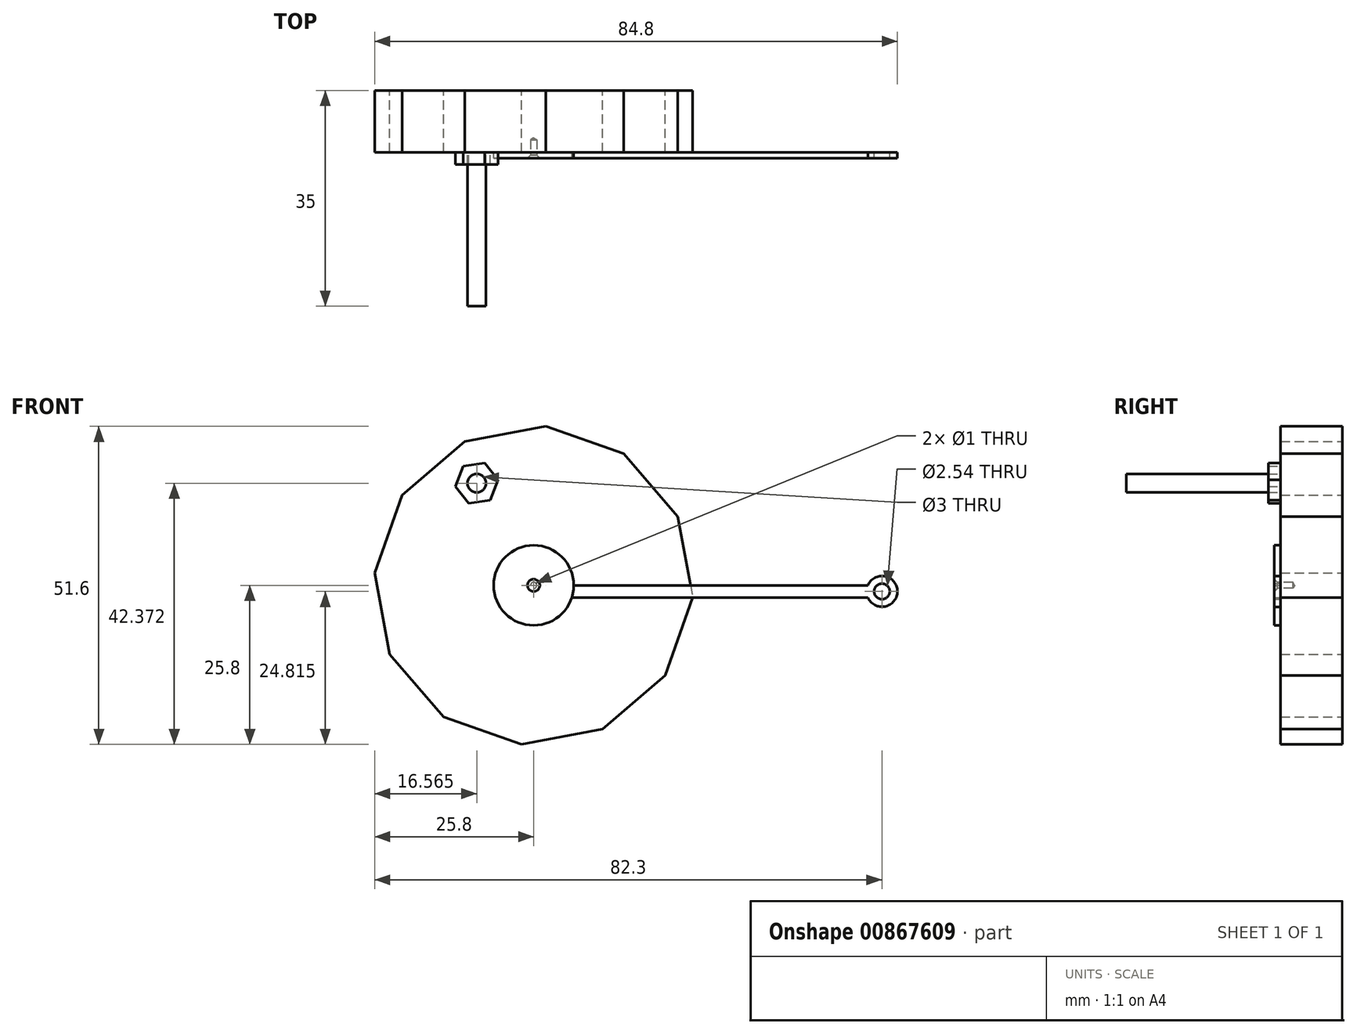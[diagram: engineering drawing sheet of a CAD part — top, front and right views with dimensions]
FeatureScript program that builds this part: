
annotation { "Feature Type Name" : "Feature", "Feature Type Description" : "" }
export const myFeature = defineFeature(function(context is Context, id is Id, definition is map)
    precondition{}
    {
        {
            var Q0;
            Q0=qCreatedBy(makeId("Front.planeOp"),FACE);
            var sketch = newSketch(context, id + "F0", { "sketchPlane" : qUnion([Q0])});
            skCircle(sketch, "E0.cCircle", {"center": v(0, 0) * mm, "radius": 25 * mm, "construction": true});
            skLineSegment(sketch, "E0.0", {"start": v(-21.35, 14.63) * mm, "end": v(-11.17, 23.35) * mm});
            skLineSegment(sketch, "E0.1", {"start": v(-11.17, 23.35) * mm, "end": v(2, 25.8) * mm});
            skLineSegment(sketch, "E0.2", {"start": v(2, 25.8) * mm, "end": v(14.63, 21.35) * mm});
            skLineSegment(sketch, "E0.3", {"start": v(14.63, 21.35) * mm, "end": v(23.35, 11.17) * mm});
            skLineSegment(sketch, "E0.4", {"start": v(23.35, 11.17) * mm, "end": v(25.8, -2) * mm});
            skLineSegment(sketch, "E0.5", {"start": v(25.8, -2) * mm, "end": v(21.35, -14.63) * mm});
            skLineSegment(sketch, "E0.6", {"start": v(21.35, -14.63) * mm, "end": v(11.17, -23.35) * mm});
            skLineSegment(sketch, "E0.7", {"start": v(11.17, -23.35) * mm, "end": v(-2, -25.8) * mm});
            skLineSegment(sketch, "E0.8", {"start": v(-2, -25.8) * mm, "end": v(-14.63, -21.35) * mm});
            skLineSegment(sketch, "E0.9", {"start": v(-14.63, -21.35) * mm, "end": v(-23.35, -11.17) * mm});
            skLineSegment(sketch, "E0.10", {"start": v(-23.35, -11.17) * mm, "end": v(-25.8, 2) * mm});
            skLineSegment(sketch, "E0.11", {"start": v(-25.8, 2) * mm, "end": v(-21.35, 14.63) * mm});
            skPoint(sketch, "E0.0.midPoint", {"position": v(-16.26, 19) * mm});
            skSolve(sketch);
        }
        {
            var Q0;
            Q0=makeQuery(id+"F0.imprint","IMPRINT",FACE,{"disambiguationData":[TD([[makeQuery(id+"F0.imprint","IMPRINT",EDGE,{"derivedFrom":sQuery(id+"F0.wireOp",EDGE,"E0.0")}),-1.0]])]});
            extrude(context, id + "F1", {"entities" : qUnion([Q0]), "depth" : 10 * mm, "offsetDistance" : 25 * mm});
        }
        {
            var Q0;
            Q0=makeQuery(id+"F1.opExtrude","CAP_FACE",FACE,{"disambiguationData":[OSD([sQuery(id+"F0.wireOp",EDGE,"E0.0"),sQuery(id+"F0.wireOp",EDGE,"E0.1"),sQuery(id+"F0.wireOp",EDGE,"E0.2"),sQuery(id+"F0.wireOp",EDGE,"E0.3"),sQuery(id+"F0.wireOp",EDGE,"E0.4"),sQuery(id+"F0.wireOp",EDGE,"E0.5"),sQuery(id+"F0.wireOp",EDGE,"E0.6"),sQuery(id+"F0.wireOp",EDGE,"E0.7"),sQuery(id+"F0.wireOp",EDGE,"E0.8"),sQuery(id+"F0.wireOp",EDGE,"E0.9"),sQuery(id+"F0.wireOp",EDGE,"E0.10"),sQuery(id+"F0.wireOp",EDGE,"E0.11")])],"isStart":false});
            var sketch = newSketch(context, id + "F2", { "sketchPlane" : qUnion([Q0])});
            skCircle(sketch, "E1", {"center": v(0, 0) * mm, "radius": 6.5 * mm});
            skLineSegment(sketch, "E2", {"start": v(6.5, 0) * mm, "end": v(56.5, 0) * mm});
            skLineSegment(sketch, "E3", {"start": v(6.2, -1.97) * mm, "end": v(56.5, -1.97) * mm});
            skLineSegment(sketch, "E4", {"start": v(56.5, 0) * mm, "end": v(56.5, -1.97) * mm});
            skCircle(sketch, "E5", {"center": v(56.5, -0.99) * mm, "radius": 2.5 * mm});
            skCircle(sketch, "E6", {"center": v(56.5, -0.99) * mm, "radius": 1.27 * mm});
            skSolve(sketch);
        }
        {
            var Q0;
            {var subQ0=sQuery(id+"F2.wireOp",EDGE,"E1");var subQ1=makeQuery(id+"F2.imprint","INTERSECT",VERTEX,{"derivedFrom":[subQ0,sQuery(id+"F2.wireOp",EDGE,"E2")]});Q0=makeQuery(id+"F2.imprint","IMPRINT",FACE,{"disambiguationData":[TD([[makeQuery(id+"F2.imprint","IMPRINT",EDGE,{"disambiguationData":[TD([[subQ1,-1.0]])],"derivedFrom":subQ0}),1.0]])]});}
            extrude(context, id + "F3", {"entities" : qUnion([Q0]), "depth" : 1 * mm, "offsetDistance" : 25 * mm});
        }
        {
            var Q0;
            {var subQ1=sQuery(id+"F2.wireOp",EDGE,"E2");var subQ6=makeQuery(id+"F1.opExtrude","CAP_EDGE",EDGE,{"disambiguationData":[OSD([sQuery(id+"F0.wireOp",EDGE,"E0.4")])],"isStart":false});var subQ8=makeQuery(id+"F2.imprint","INTERSECT",VERTEX,{"derivedFrom":[subQ6,subQ1]});Q0=makeQuery(id+"F2.imprint","IMPRINT",FACE,{"disambiguationData":[TD([[makeQuery(id+"F2.imprint","IMPRINT",EDGE,{"disambiguationData":[TD([[subQ8,-1.0]])],"derivedFrom":subQ6}),-1.0]])]});}
            var Q1;
            {var subQ0=sQuery(id+"F2.wireOp",EDGE,"E5");var subQ1=sQuery(id+"F2.wireOp",EDGE,"E2");var subQ2=makeQuery(id+"F2.imprint","INTERSECT",VERTEX,{"derivedFrom":[subQ1,subQ0]});Q1=makeQuery(id+"F2.imprint","IMPRINT",FACE,{"disambiguationData":[TD([[makeQuery(id+"F2.imprint","IMPRINT",EDGE,{"disambiguationData":[TD([[subQ2,1.0]])],"derivedFrom":subQ1}),-1.0]])]});}
            var Q2;
            {var subQ0=sQuery(id+"F2.wireOp",EDGE,"E5");var subQ1=sQuery(id+"F2.wireOp",EDGE,"E2");var subQ2=makeQuery(id+"F2.imprint","INTERSECT",VERTEX,{"derivedFrom":[subQ1,subQ0]});Q2=makeQuery(id+"F2.imprint","IMPRINT",FACE,{"disambiguationData":[TD([[makeQuery(id+"F2.imprint","IMPRINT",EDGE,{"disambiguationData":[TD([[subQ2,-1.0]])],"derivedFrom":subQ1}),1.0]])]});}
            var Q3;
            {var subQ0=sQuery(id+"F2.wireOp",EDGE,"E5");var subQ1=sQuery(id+"F2.wireOp",EDGE,"E2");var subQ2=makeQuery(id+"F2.imprint","INTERSECT",VERTEX,{"derivedFrom":[subQ1,subQ0]});Q3=makeQuery(id+"F2.imprint","IMPRINT",FACE,{"disambiguationData":[TD([[makeQuery(id+"F2.imprint","IMPRINT",EDGE,{"disambiguationData":[TD([[subQ2,-1.0]])],"derivedFrom":subQ1}),-1.0]])]});}
            extrude(context, id + "F4", {"entities" : qUnion([Q0, Q1, Q2, Q3]), "depth" : 1 * mm, "offsetDistance" : 25 * mm});
        }
        {
            var Q0;
            Q0=makeQuery(id+"F3.opExtrude","CAP_FACE",FACE,{"disambiguationData":[OSD([sQuery(id+"F2.wireOp",EDGE,"E1")])],"isStart":false});
            var sketch = newSketch(context, id + "F5", { "sketchPlane" : qUnion([Q0])});
            skPoint(sketch, "E7", {"position": v(0, 0) * mm});
            skLineSegment(sketch, "E8", {"start": v(0, 0) * mm, "end": v(0, 5.5) * mm, "construction": true});
            skLineSegment(sketch, "E9", {"start": v(0, 0) * mm, "end": v(0, -5.5) * mm, "construction": true});
            skSolve(sketch);
        }
        {
            var Q0;
            Q0=sQuery(id+"F5.wireOp",VERTEX,"E7");
            var Q1;
            Q1=makeQuery(id+"F1.opExtrude","SWEPT_BODY",BODY,{"disambiguationData":[OSD([sQuery(id+"F0.wireOp",EDGE,"E0.0"),sQuery(id+"F0.wireOp",EDGE,"E0.1"),sQuery(id+"F0.wireOp",EDGE,"E0.2"),sQuery(id+"F0.wireOp",EDGE,"E0.3"),sQuery(id+"F0.wireOp",EDGE,"E0.4"),sQuery(id+"F0.wireOp",EDGE,"E0.5"),sQuery(id+"F0.wireOp",EDGE,"E0.6"),sQuery(id+"F0.wireOp",EDGE,"E0.7"),sQuery(id+"F0.wireOp",EDGE,"E0.8"),sQuery(id+"F0.wireOp",EDGE,"E0.9"),sQuery(id+"F0.wireOp",EDGE,"E0.10"),sQuery(id+"F0.wireOp",EDGE,"E0.11")])]});
            var Q2;
            Q2=makeQuery(id+"F3.opExtrude","SWEPT_BODY",BODY,{"disambiguationData":[OSD([sQuery(id+"F2.wireOp",EDGE,"E1"),sQuery(id+"F2.wireOp",EDGE,"sMZeQURg-iBgM-XuN4-dGnC-nCPnjRgtgfTA")])]});
            hole(context, id + "F6", {"style" : HoleStyle.C_SINK, "endStyle" : HoleEndStyle.BLIND, "holeDiameter" : 1 * mm, "cSinkDiameter" : 2 * mm, "cSinkAngle" : 90 * degree, "majorDiameter" : 5 * mm, "holeDepth" : 3 * mm, "isTappedThrough" : true, "tappedDepth" : 12 * mm, "tapClearance" : 3, "startFromSketch" : true, "locations" : qUnion([Q0]), "scope" : qUnion([Q1, Q2])});
        }
        {
            var Q0;
            Q0=makeQuery(id+"F3.opExtrude","CAP_FACE",FACE,{"disambiguationData":[OSD([sQuery(id+"F2.wireOp",EDGE,"E1")])],"isStart":false});
            var sketch = newSketch(context, id + "F7", { "sketchPlane" : qUnion([Q0])});
            skCircle(sketch, "E10.0", {"center": v(0, 0) * mm, "radius": 1 * mm});
            skSolve(sketch);
        }
        {
            var Q0;
            Q0 = qSketchRegion(id + "F7", true);
            var Q1;
            Q1=makeQuery(id+"F1.opExtrude","CAP_FACE",FACE,{"disambiguationData":[OSD([sQuery(id+"F0.wireOp",EDGE,"E0.0"),sQuery(id+"F0.wireOp",EDGE,"E0.1"),sQuery(id+"F0.wireOp",EDGE,"E0.2"),sQuery(id+"F0.wireOp",EDGE,"E0.3"),sQuery(id+"F0.wireOp",EDGE,"E0.4"),sQuery(id+"F0.wireOp",EDGE,"E0.5"),sQuery(id+"F0.wireOp",EDGE,"E0.6"),sQuery(id+"F0.wireOp",EDGE,"E0.7"),sQuery(id+"F0.wireOp",EDGE,"E0.8"),sQuery(id+"F0.wireOp",EDGE,"E0.9"),sQuery(id+"F0.wireOp",EDGE,"E0.10"),sQuery(id+"F0.wireOp",EDGE,"E0.11")])],"isStart":true});
            extrude(context, id + "F8", {"entities" : qUnion([Q0]), "endBound" : BoundingType.UP_TO_SURFACE, "oppositeDirection" : true, "depth" : 25 * mm, "endBoundEntityFace" : qUnion([Q1]), "offsetDistance" : 25 * mm});
        }
        {
            var Q0;
            Q0=makeQuery(id+"F1.opExtrude","SWEPT_BODY",BODY,{"disambiguationData":[OSD([sQuery(id+"F0.wireOp",EDGE,"E0.0"),sQuery(id+"F0.wireOp",EDGE,"E0.1"),sQuery(id+"F0.wireOp",EDGE,"E0.2"),sQuery(id+"F0.wireOp",EDGE,"E0.3"),sQuery(id+"F0.wireOp",EDGE,"E0.4"),sQuery(id+"F0.wireOp",EDGE,"E0.5"),sQuery(id+"F0.wireOp",EDGE,"E0.6"),sQuery(id+"F0.wireOp",EDGE,"E0.7"),sQuery(id+"F0.wireOp",EDGE,"E0.8"),sQuery(id+"F0.wireOp",EDGE,"E0.9"),sQuery(id+"F0.wireOp",EDGE,"E0.10"),sQuery(id+"F0.wireOp",EDGE,"E0.11")])]});
            var Q1;
            Q1=makeQuery(id+"F3.opExtrude","SWEPT_BODY",BODY,{"disambiguationData":[OSD([sQuery(id+"F2.wireOp",EDGE,"E1"),sQuery(id+"F2.wireOp",EDGE,"sMZeQURg-iBgM-XuN4-dGnC-nCPnjRgtgfTA")])]});
            var Q2;
            Q2=makeQuery(id+"F8.opExtrude","SWEPT_BODY",BODY,{"disambiguationData":[OSD([sQuery(id+"F7.wireOp",EDGE,"E10.0")])]});
            booleanBodies(context, id + "F9", {"operationType" : BooleanOperationType.SUBTRACTION, "tools" : qUnion([Q0, Q1]), "targets" : qUnion([Q2]), "keepTools" : true});
        }
        {
            var Q0;
            Q0=makeQuery(id+"F1.opExtrude","CAP_FACE",FACE,{"disambiguationData":[OSD([sQuery(id+"F0.wireOp",EDGE,"E0.0"),sQuery(id+"F0.wireOp",EDGE,"E0.1"),sQuery(id+"F0.wireOp",EDGE,"E0.2"),sQuery(id+"F0.wireOp",EDGE,"E0.3"),sQuery(id+"F0.wireOp",EDGE,"E0.4"),sQuery(id+"F0.wireOp",EDGE,"E0.5"),sQuery(id+"F0.wireOp",EDGE,"E0.6"),sQuery(id+"F0.wireOp",EDGE,"E0.7"),sQuery(id+"F0.wireOp",EDGE,"E0.8"),sQuery(id+"F0.wireOp",EDGE,"E0.9"),sQuery(id+"F0.wireOp",EDGE,"E0.10"),sQuery(id+"F0.wireOp",EDGE,"E0.11")])],"isStart":false});
            var sketch = newSketch(context, id + "F10", { "sketchPlane" : qUnion([Q0])});
            skCircle(sketch, "E11", {"center": v(-9.24, 16.57) * mm, "radius": 1.5 * mm});
            skCircle(sketch, "E12.cCircle", {"center": v(-9.24, 16.57) * mm, "radius": 3.05 * mm, "construction": true});
            skLineSegment(sketch, "E12.0", {"start": v(-5.75, 17.1) * mm, "end": v(-7.04, 13.82) * mm});
            skLineSegment(sketch, "E12.1", {"start": v(-7.04, 13.82) * mm, "end": v(-10.52, 13.3) * mm});
            skLineSegment(sketch, "E12.2", {"start": v(-10.52, 13.3) * mm, "end": v(-12.72, 16.05) * mm});
            skLineSegment(sketch, "E12.3", {"start": v(-12.72, 16.05) * mm, "end": v(-11.43, 19.33) * mm});
            skLineSegment(sketch, "E12.4", {"start": v(-11.43, 19.33) * mm, "end": v(-7.95, 19.85) * mm});
            skLineSegment(sketch, "E12.5", {"start": v(-7.95, 19.85) * mm, "end": v(-5.75, 17.1) * mm});
            skPoint(sketch, "E12.0.midPoint", {"position": v(-6.4, 15.46) * mm});
            skSolve(sketch);
        }
        {
            var Q0;
            Q0=makeQuery(id+"F10.imprint","IMPRINT",FACE,{"disambiguationData":[TD([[makeQuery(id+"F10.imprint","IMPRINT",EDGE,{"derivedFrom":sQuery(id+"F10.wireOp",EDGE,"E11")}),1.0]])]});
            extrude(context, id + "F11", {"entities" : qUnion([Q0]), "depth" : 25 * mm, "offsetDistance" : 25 * mm});
        }
        {
            var Q0;
            Q0=makeQuery(id+"F10.imprint","IMPRINT",FACE,{"disambiguationData":[TD([[makeQuery(id+"F10.imprint","IMPRINT",EDGE,{"derivedFrom":sQuery(id+"F10.wireOp",EDGE,"E11")}),-1.0]])]});
            extrude(context, id + "F12", {"entities" : qUnion([Q0]), "depth" : 2 * mm, "offsetDistance" : 25 * mm});
        }
    });
